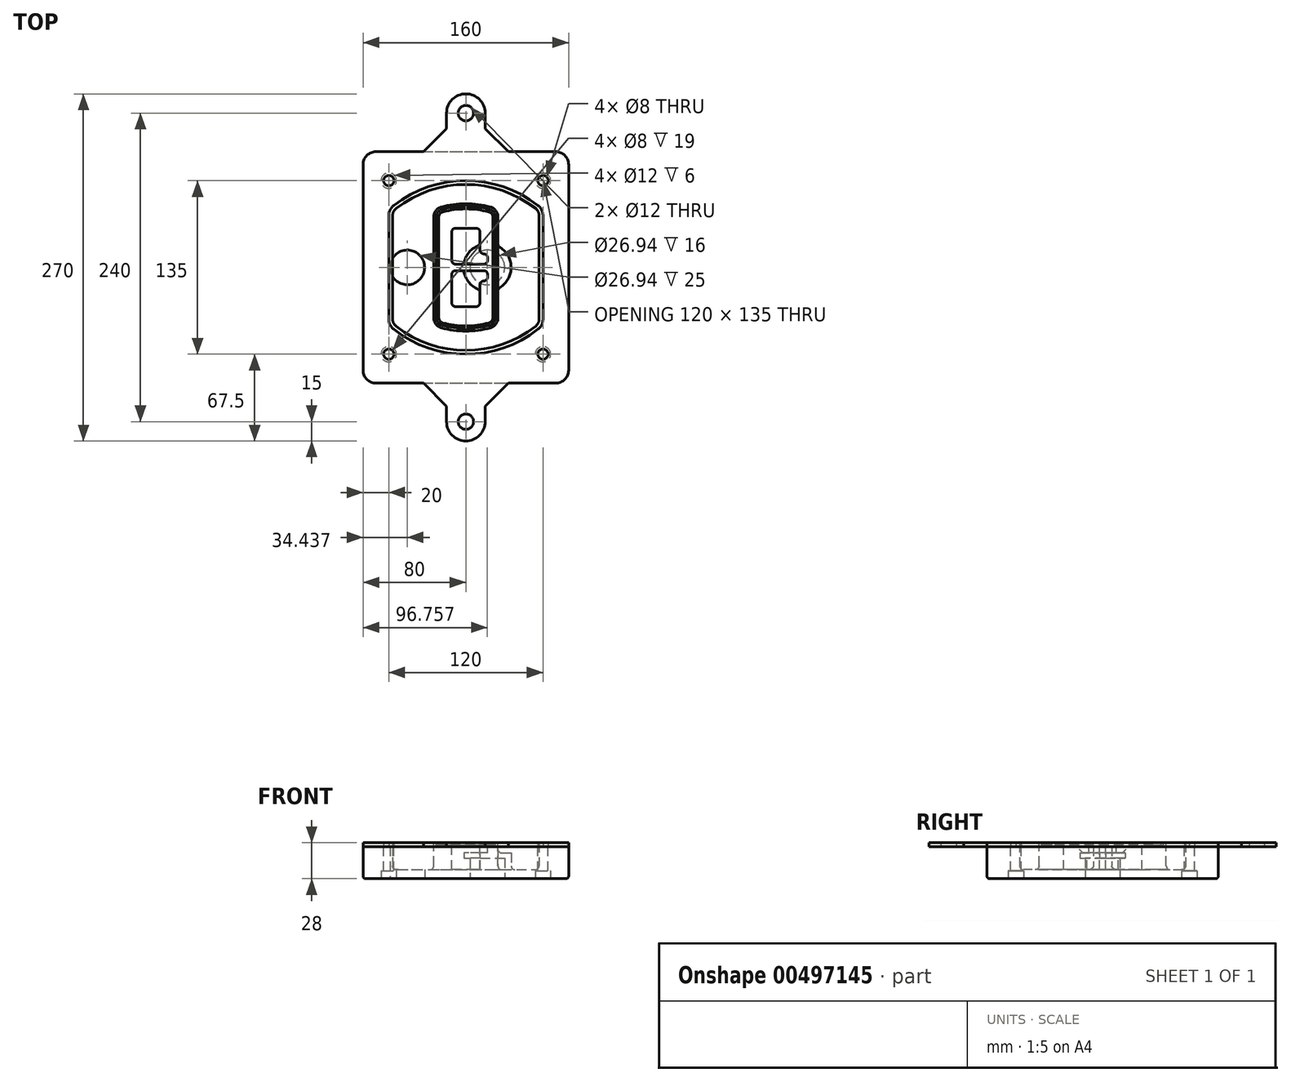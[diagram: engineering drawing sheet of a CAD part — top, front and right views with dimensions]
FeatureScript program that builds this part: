
annotation { "Feature Type Name" : "Feature", "Feature Type Description" : "" }
export const myFeature = defineFeature(function(context is Context, id is Id, definition is map)
    precondition{}
    {
        {
            var Q0;
            Q0=qCreatedBy(makeId("Top.planeOp"),FACE);
            var sketch = newSketch(context, id + "F0", { "sketchPlane" : qUnion([Q0])});
            skPoint(sketch, "E0.rect.middle", {"position": v(0, 0) * mm});
            skLineSegment(sketch, "E1.bottom", {"start": v(-70, -90) * mm, "end": v(70, -90) * mm});
            skLineSegment(sketch, "E1.top", {"start": v(-70, 90) * mm, "end": v(70, 90) * mm});
            skLineSegment(sketch, "E1.left", {"start": v(-80, -80) * mm, "end": v(-80, 80) * mm});
            skLineSegment(sketch, "E1.right", {"start": v(80, -80) * mm, "end": v(80, 80) * mm});
            skLineSegment(sketch, "E2", {"start": v(-80, 90) * mm, "end": v(80, -90) * mm, "construction": true});
            skLineSegment(sketch, "E3", {"start": v(80, 90) * mm, "end": v(-80, -90) * mm, "construction": true});
            skCircle(sketch, "E4", {"center": v(-60, 67.5) * mm, "radius": 4 * mm});
            skCircle(sketch, "E5", {"center": v(60, 67.5) * mm, "radius": 4 * mm});
            skCircle(sketch, "E6", {"center": v(60, -67.5) * mm, "radius": 4 * mm});
            skCircle(sketch, "E7", {"center": v(-60, -67.5) * mm, "radius": 4 * mm});
            skLineSegment(sketch, "E8", {"start": v(-60, 67.5) * mm, "end": v(60, 67.5) * mm, "construction": true});
            skLineSegment(sketch, "E9", {"start": v(60, 67.5) * mm, "end": v(60, -67.5) * mm, "construction": true});
            skLineSegment(sketch, "E10", {"start": v(60, -67.5) * mm, "end": v(-60, -67.5) * mm, "construction": true});
            skLineSegment(sketch, "E11", {"start": v(-60, -67.5) * mm, "end": v(-60, 67.5) * mm, "construction": true});
            skLineSegment(sketch, "E12", {"start": v(-60, 40.3) * mm, "end": v(-60, -40.3) * mm});
            skLineSegment(sketch, "E13", {"start": v(60, 40.3) * mm, "end": v(60, -40.3) * mm});
            skArc(sketch, "E14", {"start": v(56.15, 48.18) * mm, "mid": v(0, 67.5) * mm, "end": v(-56.15, 48.18) * mm});
            skArc(sketch, "E15", {"start": v(-56.15, -48.18) * mm, "mid": v(0, -67.5) * mm, "end": v(56.15, -48.18) * mm});
            skLineSegment(sketch, "E16", {"start": v(-60, 0) * mm, "end": v(60, 0) * mm, "construction": true});
            skPoint(sketch, "E17.visualSharp", {"position": v(-60, -45) * mm});
            skArc(sketch, "E17.filletArc", {"start": v(-60, -40.3) * mm, "mid": v(-58.99, -44.68) * mm, "end": v(-56.15, -48.18) * mm});
            skPoint(sketch, "E18.visualSharp", {"position": v(-60, 45) * mm});
            skArc(sketch, "E18.filletArc", {"start": v(-56.15, 48.18) * mm, "mid": v(-58.99, 44.68) * mm, "end": v(-60, 40.3) * mm});
            skPoint(sketch, "E19.visualSharp", {"position": v(60, 45) * mm});
            skArc(sketch, "E19.filletArc", {"start": v(60, 40.3) * mm, "mid": v(58.99, 44.68) * mm, "end": v(56.15, 48.18) * mm});
            skPoint(sketch, "E20.visualSharp", {"position": v(60, -45) * mm});
            skArc(sketch, "E20.filletArc", {"start": v(56.15, -48.18) * mm, "mid": v(58.99, -44.68) * mm, "end": v(60, -40.3) * mm});
            skPoint(sketch, "E21.visualSharp", {"position": v(-80, 90) * mm});
            skArc(sketch, "E21.filletArc", {"start": v(-70, 90) * mm, "mid": v(-77.07, 87.07) * mm, "end": v(-80, 80) * mm});
            skPoint(sketch, "E22.visualSharp", {"position": v(80, 90) * mm});
            skArc(sketch, "E22.filletArc", {"start": v(80, 80) * mm, "mid": v(77.07, 87.07) * mm, "end": v(70, 90) * mm});
            skPoint(sketch, "E23.visualSharp", {"position": v(80, -90) * mm});
            skArc(sketch, "E23.filletArc", {"start": v(70, -90) * mm, "mid": v(77.07, -87.07) * mm, "end": v(80, -80) * mm});
            skPoint(sketch, "E24.visualSharp", {"position": v(-80, -90) * mm});
            skArc(sketch, "E24.filletArc", {"start": v(-80, -80) * mm, "mid": v(-77.07, -87.07) * mm, "end": v(-70, -90) * mm});
            skArc(sketch, "E25.0", {"start": v(57, 40.3) * mm, "mid": v(56.3, 43.36) * mm, "end": v(54.3, 45.81) * mm});
            skLineSegment(sketch, "E25.1", {"start": v(57, 40.3) * mm, "end": v(57, -40.3) * mm});
            skArc(sketch, "E25.2", {"start": v(54.3, -45.81) * mm, "mid": v(56.3, -43.36) * mm, "end": v(57, -40.3) * mm});
            skArc(sketch, "E25.3", {"start": v(-54.3, -45.81) * mm, "mid": v(0, -64.5) * mm, "end": v(54.3, -45.81) * mm});
            skArc(sketch, "E25.4", {"start": v(-57, -40.3) * mm, "mid": v(-56.3, -43.36) * mm, "end": v(-54.3, -45.81) * mm});
            skArc(sketch, "E25.5", {"start": v(54.3, 45.81) * mm, "mid": v(0, 64.5) * mm, "end": v(-54.3, 45.81) * mm});
            skLineSegment(sketch, "E25.6", {"start": v(-57, 40.3) * mm, "end": v(-57, -40.3) * mm});
            skArc(sketch, "E25.7", {"start": v(-54.3, 45.81) * mm, "mid": v(-56.3, 43.36) * mm, "end": v(-57, 40.3) * mm});
            skArc(sketch, "E26.0", {"start": v(-58.62, 51.33) * mm, "mid": v(-62.58, 46.43) * mm, "end": v(-64, 40.3) * mm});
            skArc(sketch, "E26.1", {"start": v(58.62, 51.33) * mm, "mid": v(0, 71.5) * mm, "end": v(-58.62, 51.33) * mm});
            skArc(sketch, "E26.2", {"start": v(64, 40.3) * mm, "mid": v(62.58, 46.43) * mm, "end": v(58.62, 51.33) * mm});
            skLineSegment(sketch, "E26.3", {"start": v(64, 40.3) * mm, "end": v(64, -40.3) * mm});
            skArc(sketch, "E26.4", {"start": v(58.62, -51.33) * mm, "mid": v(62.58, -46.43) * mm, "end": v(64, -40.3) * mm});
            skLineSegment(sketch, "E26.5", {"start": v(-64, 40.3) * mm, "end": v(-64, -40.3) * mm});
            skArc(sketch, "E26.6", {"start": v(-58.62, -51.33) * mm, "mid": v(0, -71.5) * mm, "end": v(58.62, -51.33) * mm});
            skArc(sketch, "E26.7", {"start": v(-64, -40.3) * mm, "mid": v(-62.58, -46.43) * mm, "end": v(-58.62, -51.33) * mm});
            skSolve(sketch);
        }
        {
            var Q0;
            Q0=makeQuery(id+"F0.imprint","IMPRINT",FACE,{"disambiguationData":[TD([[makeQuery(id+"F0.imprint","IMPRINT",EDGE,{"derivedFrom":sQuery(id+"F0.wireOp",EDGE,"E1.bottom")}),1.0]])]});
            var Q1;
            Q1=makeQuery(id+"F0.imprint","IMPRINT",FACE,{"disambiguationData":[TD([[makeQuery(id+"F0.imprint","IMPRINT",EDGE,{"derivedFrom":sQuery(id+"F0.wireOp",EDGE,"E12")}),1.0]])]});
            var Q2;
            Q2=makeQuery(id+"F0.imprint","IMPRINT",FACE,{"disambiguationData":[TD([[makeQuery(id+"F0.imprint","IMPRINT",EDGE,{"derivedFrom":sQuery(id+"F0.wireOp",EDGE,"E25.0")}),1.0]])]});
            var Q3;
            Q3=makeQuery(id+"F0.imprint","IMPRINT",FACE,{"disambiguationData":[TD([[makeQuery(id+"F0.imprint","IMPRINT",EDGE,{"derivedFrom":sQuery(id+"F0.wireOp",EDGE,"E12")}),-1.0]])]});
            extrude(context, id + "F1", {"entities" : qUnion([Q0, Q1, Q2, Q3]), "oppositeDirection" : true, "depth" : 25 * mm});
        }
        {
            var Q0;
            Q0=makeQuery(id+"F0.imprint","IMPRINT",FACE,{"disambiguationData":[TD([[makeQuery(id+"F0.imprint","IMPRINT",EDGE,{"derivedFrom":sQuery(id+"F0.wireOp",EDGE,"E12")}),1.0]])]});
            extrude(context, id + "F2", {"entities" : qUnion([Q0]), "operationType" : NewBodyOperationType.ADD, "depth" : 3 * mm});
        }
        {
            var Q0;
            Q0=makeQuery(id+"F0.imprint","IMPRINT",FACE,{"disambiguationData":[TD([[makeQuery(id+"F0.imprint","IMPRINT",EDGE,{"derivedFrom":sQuery(id+"F0.wireOp",EDGE,"E25.0")}),1.0]])]});
            extrude(context, id + "F3", {"entities" : qUnion([Q0]), "operationType" : NewBodyOperationType.REMOVE, "oppositeDirection" : true, "depth" : 18 * mm});
        }
        {
            var Q0;
            Q0=makeQuery(id+"F2.opExtrude","CAP_FACE",FACE,{"disambiguationData":[OSD([sQuery(id+"F0.wireOp",EDGE,"E12"),sQuery(id+"F0.wireOp",EDGE,"E13"),sQuery(id+"F0.wireOp",EDGE,"E14"),sQuery(id+"F0.wireOp",EDGE,"E15"),sQuery(id+"F0.wireOp",EDGE,"E17.filletArc"),sQuery(id+"F0.wireOp",EDGE,"E18.filletArc"),sQuery(id+"F0.wireOp",EDGE,"E19.filletArc"),sQuery(id+"F0.wireOp",EDGE,"E20.filletArc"),sQuery(id+"F0.wireOp",EDGE,"E25.0"),sQuery(id+"F0.wireOp",EDGE,"E25.1"),sQuery(id+"F0.wireOp",EDGE,"E25.2"),sQuery(id+"F0.wireOp",EDGE,"E25.3"),sQuery(id+"F0.wireOp",EDGE,"E25.4"),sQuery(id+"F0.wireOp",EDGE,"E25.5"),sQuery(id+"F0.wireOp",EDGE,"E25.6"),sQuery(id+"F0.wireOp",EDGE,"E25.7")])],"isStart":false});
            var sketch = newSketch(context, id + "F4", { "sketchPlane" : qUnion([Q0])});
            skArc(sketch, "E27.0", {"start": v(-19.08, -46.97) * mm, "mid": v(0, -49.5) * mm, "end": v(19.08, -46.97) * mm});
            skArc(sketch, "E28.0", {"start": v(19.08, 46.97) * mm, "mid": v(0, 49.5) * mm, "end": v(-19.08, 46.97) * mm});
            skLineSegment(sketch, "E29", {"start": v(-25, 39.25) * mm, "end": v(-25, -39.25) * mm});
            skLineSegment(sketch, "E30", {"start": v(25, 39.25) * mm, "end": v(25, -39.25) * mm});
            skLineSegment(sketch, "E31", {"start": v(-25, 45.1) * mm, "end": v(25, 45.1) * mm, "construction": true});
            skLineSegment(sketch, "E32", {"start": v(-25, -45.1) * mm, "end": v(25, -45.1) * mm, "construction": true});
            skPoint(sketch, "E33.visualSharp", {"position": v(-25, 45.1) * mm});
            skArc(sketch, "E33.filletArc", {"start": v(-19.08, 46.97) * mm, "mid": v(-23.35, 44.11) * mm, "end": v(-25, 39.25) * mm});
            skPoint(sketch, "E34.visualSharp", {"position": v(25, 45.1) * mm});
            skArc(sketch, "E34.filletArc", {"start": v(25, 39.25) * mm, "mid": v(23.35, 44.11) * mm, "end": v(19.08, 46.97) * mm});
            skPoint(sketch, "E35.visualSharp", {"position": v(25, -45.1) * mm});
            skArc(sketch, "E35.filletArc", {"start": v(19.08, -46.97) * mm, "mid": v(23.35, -44.11) * mm, "end": v(25, -39.25) * mm});
            skPoint(sketch, "E36.visualSharp", {"position": v(-25, -45.1) * mm});
            skArc(sketch, "E36.filletArc", {"start": v(-25, -39.25) * mm, "mid": v(-23.35, -44.11) * mm, "end": v(-19.08, -46.97) * mm});
            skArc(sketch, "E37.0", {"start": v(54.3, 45.81) * mm, "mid": v(0, 64.5) * mm, "end": v(-54.3, 45.81) * mm});
            skArc(sketch, "E37.1", {"start": v(-54.3, 45.81) * mm, "mid": v(-56.3, 43.36) * mm, "end": v(-57, 40.3) * mm});
            skLineSegment(sketch, "E37.2", {"start": v(-57, 40.3) * mm, "end": v(-57, -40.3) * mm});
            skArc(sketch, "E37.3", {"start": v(-57, -40.3) * mm, "mid": v(-56.3, -43.36) * mm, "end": v(-54.3, -45.81) * mm});
            skArc(sketch, "E37.4", {"start": v(-54.3, -45.81) * mm, "mid": v(0, -64.5) * mm, "end": v(54.3, -45.81) * mm});
            skArc(sketch, "E37.5", {"start": v(54.3, -45.81) * mm, "mid": v(56.3, -43.36) * mm, "end": v(57, -40.3) * mm});
            skLineSegment(sketch, "E37.6", {"start": v(57, 40.3) * mm, "end": v(57, -40.3) * mm});
            skArc(sketch, "E37.7", {"start": v(57, 40.3) * mm, "mid": v(56.3, 43.36) * mm, "end": v(54.3, 45.81) * mm});
            skLineSegment(sketch, "E38.0", {"start": v(23, 39.25) * mm, "end": v(23, -39.25) * mm});
            skArc(sketch, "E38.1", {"start": v(18.56, -45.04) * mm, "mid": v(21.76, -42.9) * mm, "end": v(23, -39.25) * mm});
            skArc(sketch, "E38.2", {"start": v(-18.56, -45.04) * mm, "mid": v(0, -47.5) * mm, "end": v(18.56, -45.04) * mm});
            skArc(sketch, "E38.3", {"start": v(-23, -39.25) * mm, "mid": v(-21.76, -42.9) * mm, "end": v(-18.56, -45.04) * mm});
            skLineSegment(sketch, "E38.4", {"start": v(-23, 39.25) * mm, "end": v(-23, -39.25) * mm});
            skArc(sketch, "E38.5", {"start": v(23, 39.25) * mm, "mid": v(21.76, 42.9) * mm, "end": v(18.56, 45.04) * mm});
            skArc(sketch, "E38.6", {"start": v(-18.56, 45.04) * mm, "mid": v(-21.76, 42.9) * mm, "end": v(-23, 39.25) * mm});
            skArc(sketch, "E38.7", {"start": v(18.56, 45.04) * mm, "mid": v(0, 47.5) * mm, "end": v(-18.56, 45.04) * mm});
            skArc(sketch, "E39.0", {"start": v(21, 39.25) * mm, "mid": v(20.18, 41.68) * mm, "end": v(18.04, 43.1) * mm});
            skLineSegment(sketch, "E39.1", {"start": v(21, 39.25) * mm, "end": v(21, -39.25) * mm});
            skArc(sketch, "E39.2", {"start": v(18.04, -43.1) * mm, "mid": v(20.18, -41.68) * mm, "end": v(21, -39.25) * mm});
            skArc(sketch, "E39.3", {"start": v(-18.04, -43.1) * mm, "mid": v(0, -45.5) * mm, "end": v(18.04, -43.1) * mm});
            skArc(sketch, "E39.4", {"start": v(-21, -39.25) * mm, "mid": v(-20.18, -41.68) * mm, "end": v(-18.04, -43.1) * mm});
            skArc(sketch, "E39.5", {"start": v(18.04, 43.1) * mm, "mid": v(0, 45.5) * mm, "end": v(-18.04, 43.1) * mm});
            skLineSegment(sketch, "E39.6", {"start": v(-21, 39.25) * mm, "end": v(-21, -39.25) * mm});
            skArc(sketch, "E39.7", {"start": v(-18.04, 43.1) * mm, "mid": v(-20.18, 41.68) * mm, "end": v(-21, 39.25) * mm});
            skLineSegment(sketch, "E40", {"start": v(-25, 0) * mm, "end": v(25, 0) * mm, "construction": true});
            skLineSegment(sketch, "E41", {"start": v(-11, 5.5) * mm, "end": v(-11, 27.5) * mm});
            skLineSegment(sketch, "E42", {"start": v(-8, 30.5) * mm, "end": v(8, 30.5) * mm});
            skLineSegment(sketch, "E43", {"start": v(11, 27.5) * mm, "end": v(11, 13.5) * mm});
            skLineSegment(sketch, "E44", {"start": v(14, 10.5) * mm, "end": v(14, 10.5) * mm});
            skLineSegment(sketch, "E45", {"start": v(17, 7.5) * mm, "end": v(17, 5.5) * mm});
            skLineSegment(sketch, "E46", {"start": v(14, 2.5) * mm, "end": v(-8, 2.5) * mm});
            skPoint(sketch, "E47.visualSharp", {"position": v(-11, 30.5) * mm});
            skArc(sketch, "E47.filletArc", {"start": v(-8, 30.5) * mm, "mid": v(-10.12, 29.62) * mm, "end": v(-11, 27.5) * mm});
            skPoint(sketch, "E48.visualSharp", {"position": v(11, 30.5) * mm});
            skArc(sketch, "E48.filletArc", {"start": v(11, 27.5) * mm, "mid": v(10.12, 29.62) * mm, "end": v(8, 30.5) * mm});
            skPoint(sketch, "E49.visualSharp", {"position": v(11, 10.5) * mm});
            skArc(sketch, "E49.filletArc", {"start": v(11, 13.5) * mm, "mid": v(11.88, 11.38) * mm, "end": v(14, 10.5) * mm});
            skPoint(sketch, "E50.visualSharp", {"position": v(17, 10.5) * mm});
            skArc(sketch, "E50.filletArc", {"start": v(17, 7.5) * mm, "mid": v(16.12, 9.62) * mm, "end": v(14, 10.5) * mm});
            skPoint(sketch, "E51.visualSharp", {"position": v(17, 2.5) * mm});
            skArc(sketch, "E51.filletArc", {"start": v(14, 2.5) * mm, "mid": v(16.12, 3.38) * mm, "end": v(17, 5.5) * mm});
            skPoint(sketch, "E52.visualSharp", {"position": v(-11, 2.5) * mm});
            skArc(sketch, "E52.filletArc", {"start": v(-11, 5.5) * mm, "mid": v(-10.12, 3.38) * mm, "end": v(-8, 2.5) * mm});
            skLineSegment(sketch, "E53.0.MirrorCS", {"start": v(14, -2.5) * mm, "end": v(-8, -2.5) * mm});
            skArc(sketch, "E54.0.MirrorCS", {"start": v(-11, -5.5) * mm, "mid": v(-10.12, -3.38) * mm, "end": v(-8, -2.5) * mm});
            skLineSegment(sketch, "E55.0.MirrorCS", {"start": v(-11, -5.5) * mm, "end": v(-11, -27.5) * mm});
            skArc(sketch, "E56.0.MirrorCS", {"start": v(-8, -30.5) * mm, "mid": v(-10.12, -29.62) * mm, "end": v(-11, -27.5) * mm});
            skLineSegment(sketch, "E57.0.MirrorCS", {"start": v(-8, -30.5) * mm, "end": v(8, -30.5) * mm});
            skArc(sketch, "E58.0.MirrorCS", {"start": v(11, -27.5) * mm, "mid": v(10.12, -29.62) * mm, "end": v(8, -30.5) * mm});
            skLineSegment(sketch, "E59.0.MirrorCS", {"start": v(11, -27.5) * mm, "end": v(11, -13.5) * mm});
            skArc(sketch, "E60.0.MirrorCS", {"start": v(11, -13.5) * mm, "mid": v(11.88, -11.38) * mm, "end": v(14, -10.5) * mm});
            skArc(sketch, "E61.0.MirrorCS", {"start": v(17, -7.5) * mm, "mid": v(16.12, -9.62) * mm, "end": v(14, -10.5) * mm});
            skLineSegment(sketch, "E62.0.MirrorCS", {"start": v(17, -7.5) * mm, "end": v(17, -5.5) * mm});
            skArc(sketch, "E63.0.MirrorCS", {"start": v(14, -2.5) * mm, "mid": v(16.12, -3.38) * mm, "end": v(17, -5.5) * mm});
            skSolve(sketch);
        }
        {
            var Q0;
            Q0=makeQuery(id+"F4.imprint","IMPRINT",FACE,{"disambiguationData":[TD([[makeQuery(id+"F4.imprint","IMPRINT",EDGE,{"derivedFrom":sQuery(id+"F4.wireOp",EDGE,"E27.0")}),1.0]])]});
            var Q1;
            Q1=makeQuery(id+"F4.imprint","IMPRINT",FACE,{"disambiguationData":[TD([[makeQuery(id+"F4.imprint","IMPRINT",EDGE,{"derivedFrom":sQuery(id+"F4.wireOp",EDGE,"E38.0")}),-1.0]])]});
            var Q2;
            Q2=makeQuery(id+"F4.imprint","IMPRINT",FACE,{"disambiguationData":[TD([[makeQuery(id+"F4.imprint","IMPRINT",EDGE,{"derivedFrom":sQuery(id+"F4.wireOp",EDGE,"E39.0")}),1.0]])]});
            extrude(context, id + "F5", {"entities" : qUnion([Q0, Q1, Q2]), "operationType" : NewBodyOperationType.ADD, "endBound" : BoundingType.UP_TO_NEXT, "oppositeDirection" : true, "depth" : 25 * mm});
        }
        {
            var Q0;
            Q0=makeQuery(id+"F4.imprint","IMPRINT",FACE,{"disambiguationData":[TD([[makeQuery(id+"F4.imprint","IMPRINT",EDGE,{"derivedFrom":sQuery(id+"F4.wireOp",EDGE,"E38.0")}),-1.0]])]});
            extrude(context, id + "F6", {"entities" : qUnion([Q0]), "operationType" : NewBodyOperationType.REMOVE, "oppositeDirection" : true, "depth" : 2 * mm});
        }
        {
            var Q0;
            Q0=makeQuery(id+"F1.opExtrude","CAP_FACE",FACE,{"disambiguationData":[OSD([sQuery(id+"F0.wireOp",EDGE,"E1.bottom"),sQuery(id+"F0.wireOp",EDGE,"E1.top"),sQuery(id+"F0.wireOp",EDGE,"E1.left"),sQuery(id+"F0.wireOp",EDGE,"E1.right"),sQuery(id+"F0.wireOp",EDGE,"E4"),sQuery(id+"F0.wireOp",EDGE,"E5"),sQuery(id+"F0.wireOp",EDGE,"E6"),sQuery(id+"F0.wireOp",EDGE,"E7"),sQuery(id+"F0.wireOp",EDGE,"E21.filletArc"),sQuery(id+"F0.wireOp",EDGE,"E22.filletArc"),sQuery(id+"F0.wireOp",EDGE,"E23.filletArc"),sQuery(id+"F0.wireOp",EDGE,"E24.filletArc")])],"isStart":false});
            var sketch = newSketch(context, id + "F7", { "sketchPlane" : qUnion([Q0])});
            skCircle(sketch, "E64", {"center": v(16.76, 0) * mm, "radius": 13.47 * mm});
            skCircle(sketch, "E65", {"center": v(-45.56, 0) * mm, "radius": 13.47 * mm});
            skLineSegment(sketch, "E66", {"start": v(80, 0) * mm, "end": v(-80, 0) * mm});
            skCircle(sketch, "E67", {"center": v(16.76, 0) * mm, "radius": 18.47 * mm});
            skCircle(sketch, "E68", {"center": v(60, -67.5) * mm, "radius": 6 * mm});
            skCircle(sketch, "E69", {"center": v(-60, -67.5) * mm, "radius": 6 * mm});
            skCircle(sketch, "E70", {"center": v(-60, 67.5) * mm, "radius": 6 * mm});
            skCircle(sketch, "E71", {"center": v(60, 67.5) * mm, "radius": 6 * mm});
            skSolve(sketch);
        }
        {
            var Q0;
            {var subQ1=sQuery(id+"F7.wireOp",EDGE,"E66");var subQ4=sQuery(id+"F7.wireOp",EDGE,"E64");var subQ6=makeQuery(id+"F7.imprint","INTERSECT",VERTEX,{"disambiguationData":[OD(0.0)],"derivedFrom":[subQ4,subQ1]});Q0=makeQuery(id+"F7.imprint","IMPRINT",FACE,{"disambiguationData":[TD([[makeQuery(id+"F7.imprint","IMPRINT",EDGE,{"disambiguationData":[TD([[subQ6,-1.0]])],"derivedFrom":subQ4}),-1.0]])]});}
            var Q1;
            {var subQ0=sQuery(id+"F7.wireOp",EDGE,"E66");var subQ1=sQuery(id+"F7.wireOp",EDGE,"E64");var subQ3=makeQuery(id+"F7.imprint","INTERSECT",VERTEX,{"disambiguationData":[OD(0.0)],"derivedFrom":[subQ1,subQ0]});Q1=makeQuery(id+"F7.imprint","IMPRINT",FACE,{"disambiguationData":[TD([[makeQuery(id+"F7.imprint","IMPRINT",EDGE,{"disambiguationData":[TD([[subQ3,-1.0]])],"derivedFrom":subQ1}),1.0]])]});}
            var Q2;
            {var subQ0=sQuery(id+"F7.wireOp",EDGE,"E66");var subQ1=sQuery(id+"F7.wireOp",EDGE,"E64");var subQ3=makeQuery(id+"F7.imprint","INTERSECT",VERTEX,{"disambiguationData":[OD(0.0)],"derivedFrom":[subQ1,subQ0]});Q2=makeQuery(id+"F7.imprint","IMPRINT",FACE,{"disambiguationData":[TD([[makeQuery(id+"F7.imprint","IMPRINT",EDGE,{"disambiguationData":[TD([[subQ3,1.0]])],"derivedFrom":subQ1}),1.0]])]});}
            var Q3;
            {var subQ1=sQuery(id+"F7.wireOp",EDGE,"E66");var subQ4=sQuery(id+"F7.wireOp",EDGE,"E64");var subQ6=makeQuery(id+"F7.imprint","INTERSECT",VERTEX,{"disambiguationData":[OD(0.0)],"derivedFrom":[subQ4,subQ1]});Q3=makeQuery(id+"F7.imprint","IMPRINT",FACE,{"disambiguationData":[TD([[makeQuery(id+"F7.imprint","IMPRINT",EDGE,{"disambiguationData":[TD([[subQ6,1.0]])],"derivedFrom":subQ4}),-1.0]])]});}
            extrude(context, id + "F8", {"entities" : qUnion([Q0, Q1, Q2, Q3]), "operationType" : NewBodyOperationType.ADD, "oppositeDirection" : true, "depth" : 20 * mm});
        }
        {
            var Q0;
            {var subQ0=sQuery(id+"F7.wireOp",EDGE,"E66");var subQ1=sQuery(id+"F7.wireOp",EDGE,"E64");var subQ3=makeQuery(id+"F7.imprint","INTERSECT",VERTEX,{"disambiguationData":[OD(0.0)],"derivedFrom":[subQ1,subQ0]});Q0=makeQuery(id+"F7.imprint","IMPRINT",FACE,{"disambiguationData":[TD([[makeQuery(id+"F7.imprint","IMPRINT",EDGE,{"disambiguationData":[TD([[subQ3,-1.0]])],"derivedFrom":subQ1}),1.0]])]});}
            var Q1;
            {var subQ0=sQuery(id+"F7.wireOp",EDGE,"E66");var subQ1=sQuery(id+"F7.wireOp",EDGE,"E64");var subQ3=makeQuery(id+"F7.imprint","INTERSECT",VERTEX,{"disambiguationData":[OD(0.0)],"derivedFrom":[subQ1,subQ0]});Q1=makeQuery(id+"F7.imprint","IMPRINT",FACE,{"disambiguationData":[TD([[makeQuery(id+"F7.imprint","IMPRINT",EDGE,{"disambiguationData":[TD([[subQ3,1.0]])],"derivedFrom":subQ1}),1.0]])]});}
            extrude(context, id + "F9", {"entities" : qUnion([Q0, Q1]), "operationType" : NewBodyOperationType.REMOVE, "oppositeDirection" : true, "depth" : 16 * mm});
        }
        {
            var Q0;
            {var subQ0=sQuery(id+"F7.wireOp",EDGE,"E66");var subQ1=sQuery(id+"F7.wireOp",EDGE,"E65");var subQ3=makeQuery(id+"F7.imprint","INTERSECT",VERTEX,{"disambiguationData":[OD(0.0)],"derivedFrom":[subQ1,subQ0]});Q0=makeQuery(id+"F7.imprint","IMPRINT",FACE,{"disambiguationData":[TD([[makeQuery(id+"F7.imprint","IMPRINT",EDGE,{"disambiguationData":[TD([[subQ3,-1.0]])],"derivedFrom":subQ1}),1.0]])]});}
            var Q1;
            {var subQ0=sQuery(id+"F7.wireOp",EDGE,"E66");var subQ1=sQuery(id+"F7.wireOp",EDGE,"E65");var subQ3=makeQuery(id+"F7.imprint","INTERSECT",VERTEX,{"disambiguationData":[OD(0.0)],"derivedFrom":[subQ1,subQ0]});Q1=makeQuery(id+"F7.imprint","IMPRINT",FACE,{"disambiguationData":[TD([[makeQuery(id+"F7.imprint","IMPRINT",EDGE,{"disambiguationData":[TD([[subQ3,1.0]])],"derivedFrom":subQ1}),1.0]])]});}
            extrude(context, id + "F10", {"entities" : qUnion([Q0, Q1]), "operationType" : NewBodyOperationType.REMOVE, "oppositeDirection" : true, "depth" : 25 * mm});
        }
        {
            var Q0;
            Q0=makeQuery(id+"F7.imprint","IMPRINT",FACE,{"disambiguationData":[TD([[makeQuery(id+"F7.imprint","IMPRINT",EDGE,{"derivedFrom":sQuery(id+"F7.wireOp",EDGE,"E68")}),1.0]])]});
            var Q1;
            Q1=makeQuery(id+"F7.imprint","IMPRINT",FACE,{"disambiguationData":[TD([[makeQuery(id+"F7.imprint","IMPRINT",EDGE,{"derivedFrom":makeQuery(id+"F1.opExtrude","CAP_EDGE",EDGE,{"disambiguationData":[OSD([sQuery(id+"F0.wireOp",EDGE,"E5")])],"isStart":false})}),-1.0]])]});
            var Q2;
            Q2=makeQuery(id+"F7.imprint","IMPRINT",FACE,{"disambiguationData":[TD([[makeQuery(id+"F7.imprint","IMPRINT",EDGE,{"derivedFrom":sQuery(id+"F7.wireOp",EDGE,"E69")}),1.0]])]});
            var Q3;
            Q3=makeQuery(id+"F7.imprint","IMPRINT",FACE,{"disambiguationData":[TD([[makeQuery(id+"F7.imprint","IMPRINT",EDGE,{"derivedFrom":makeQuery(id+"F1.opExtrude","CAP_EDGE",EDGE,{"disambiguationData":[OSD([sQuery(id+"F0.wireOp",EDGE,"E4")])],"isStart":false})}),-1.0]])]});
            var Q4;
            Q4=makeQuery(id+"F7.imprint","IMPRINT",FACE,{"disambiguationData":[TD([[makeQuery(id+"F7.imprint","IMPRINT",EDGE,{"derivedFrom":sQuery(id+"F7.wireOp",EDGE,"E70")}),1.0]])]});
            var Q5;
            Q5=makeQuery(id+"F7.imprint","IMPRINT",FACE,{"disambiguationData":[TD([[makeQuery(id+"F7.imprint","IMPRINT",EDGE,{"derivedFrom":makeQuery(id+"F1.opExtrude","CAP_EDGE",EDGE,{"disambiguationData":[OSD([sQuery(id+"F0.wireOp",EDGE,"E7")])],"isStart":false})}),-1.0]])]});
            var Q6;
            Q6=makeQuery(id+"F7.imprint","IMPRINT",FACE,{"disambiguationData":[TD([[makeQuery(id+"F7.imprint","IMPRINT",EDGE,{"derivedFrom":sQuery(id+"F7.wireOp",EDGE,"E71")}),1.0]])]});
            var Q7;
            Q7=makeQuery(id+"F7.imprint","IMPRINT",FACE,{"disambiguationData":[TD([[makeQuery(id+"F7.imprint","IMPRINT",EDGE,{"derivedFrom":makeQuery(id+"F1.opExtrude","CAP_EDGE",EDGE,{"disambiguationData":[OSD([sQuery(id+"F0.wireOp",EDGE,"E6")])],"isStart":false})}),-1.0]])]});
            extrude(context, id + "F11", {"entities" : qUnion([Q0, Q1, Q2, Q3, Q4, Q5, Q6, Q7]), "operationType" : NewBodyOperationType.REMOVE, "oppositeDirection" : true, "depth" : 6 * mm});
        }
        {
            var Q0;
            Q0=makeQuery(id+"F9.boolean.opBoolean","COPY",FACE,{"derivedFrom":makeQuery(id+"F9.opExtrude","CAP_FACE",FACE,{"disambiguationData":[OSD([sQuery(id+"F7.wireOp",EDGE,"E64")])],"isStart":false})});
            var sketch = newSketch(context, id + "F12", { "sketchPlane" : qUnion([Q0])});
            skArc(sketch, "E72.0", {"start": v(11, 17.55) * mm, "mid": v(2.57, 11.82) * mm, "end": v(-1.54, 2.5) * mm});
            skArc(sketch, "E72.1", {"start": v(-1.54, -2.5) * mm, "mid": v(2.57, -11.82) * mm, "end": v(11, -17.55) * mm});
            skLineSegment(sketch, "E73", {"start": v(-1.54, -2.5) * mm, "end": v(14, -2.5) * mm});
            skLineSegment(sketch, "E74.0", {"start": v(14, 2.5) * mm, "end": v(-1.54, 2.5) * mm});
            skArc(sketch, "E74.1", {"start": v(14, 2.5) * mm, "mid": v(16.12, 3.38) * mm, "end": v(17, 5.5) * mm});
            skLineSegment(sketch, "E74.2", {"start": v(17, 7.5) * mm, "end": v(17, 5.5) * mm});
            skArc(sketch, "E74.3", {"start": v(17, 7.5) * mm, "mid": v(16.12, 9.62) * mm, "end": v(14, 10.5) * mm});
            skArc(sketch, "E74.4", {"start": v(11, 13.5) * mm, "mid": v(11.88, 11.38) * mm, "end": v(14, 10.5) * mm});
            skLineSegment(sketch, "E74.5", {"start": v(11, 17.55) * mm, "end": v(11, 13.5) * mm});
            skLineSegment(sketch, "E74.7", {"start": v(14, -2.5) * mm, "end": v(-1.54, -2.5) * mm});
            skArc(sketch, "E74.8", {"start": v(14, -2.5) * mm, "mid": v(16.12, -3.38) * mm, "end": v(17, -5.5) * mm});
            skLineSegment(sketch, "E74.9", {"start": v(17, -7.5) * mm, "end": v(17, -5.5) * mm});
            skArc(sketch, "E74.10", {"start": v(17, -7.5) * mm, "mid": v(16.12, -9.62) * mm, "end": v(14, -10.5) * mm});
            skArc(sketch, "E74.11", {"start": v(11, -13.5) * mm, "mid": v(11.88, -11.38) * mm, "end": v(14, -10.5) * mm});
            skLineSegment(sketch, "E74.12", {"start": v(11, -17.55) * mm, "end": v(11, -13.5) * mm});
            skPoint(sketch, "E75.orphan", {"position": v(11, -27.5) * mm});
            skPoint(sketch, "E76.orphan", {"position": v(-8, -2.5) * mm});
            skPoint(sketch, "E77.orphan", {"position": v(-8, 2.5) * mm});
            skPoint(sketch, "E78.orphan", {"position": v(11, 27.5) * mm});
            skSolve(sketch);
        }
        {
            var Q0;
            {var subQ7=sQuery(id+"F12.wireOp",EDGE,"E72.0");var subQ14=sQuery(id+"F12.wireOp",EDGE,"E72.1");var subQ16=sQuery(id+"F12.wireOp",EDGE,"E74.1");var subQ18=sQuery(id+"F12.wireOp",EDGE,"E74.8");Q0=qUnion([makeQuery(id+"F12.imprint","IMPRINT",FACE,{"disambiguationData":[TD([[makeQuery(id+"F12.imprint","IMPRINT",EDGE,{"derivedFrom":subQ7}),1.0]])]}),makeQuery(id+"F12.imprint","IMPRINT",FACE,{"disambiguationData":[TD([[makeQuery(id+"F12.imprint","IMPRINT",EDGE,{"derivedFrom":subQ14}),1.0]])]}),makeQuery(id+"F12.imprint","IMPRINT",FACE,{"disambiguationData":[TD([[makeQuery(id+"F12.imprint","IMPRINT",EDGE,{"derivedFrom":subQ16}),1.0]])]}),makeQuery(id+"F12.imprint","IMPRINT",FACE,{"disambiguationData":[TD([[makeQuery(id+"F12.imprint","IMPRINT",EDGE,{"derivedFrom":subQ18}),-1.0]])]})]);}
            var Q1;
            Q1=makeQuery(id+"F5.boolean.opBoolean","SPLIT",FACE,{"disambiguationData":[TD([makeQuery(id+"F5.opExtrude","SWEPT_FACE",FACE,{"disambiguationData":[OSD([sQuery(id+"F4.wireOp",EDGE,"E41")])]})])],"derivedFrom":makeQuery(id+"F3.boolean.opBoolean","COPY",FACE,{"derivedFrom":makeQuery(id+"F3.opExtrude","CAP_FACE",FACE,{"disambiguationData":[OSD([sQuery(id+"F0.wireOp",EDGE,"E25.0"),sQuery(id+"F0.wireOp",EDGE,"E25.1"),sQuery(id+"F0.wireOp",EDGE,"E25.2"),sQuery(id+"F0.wireOp",EDGE,"E25.3"),sQuery(id+"F0.wireOp",EDGE,"E25.4"),sQuery(id+"F0.wireOp",EDGE,"E25.5"),sQuery(id+"F0.wireOp",EDGE,"E25.6"),sQuery(id+"F0.wireOp",EDGE,"E25.7")])],"isStart":false})})});
            extrude(context, id + "F13", {"entities" : qUnion([Q0]), "operationType" : NewBodyOperationType.REMOVE, "endBound" : BoundingType.UP_TO_SURFACE, "endBoundEntityFace" : qUnion([Q1]), "depth" : 25 * mm});
        }
        {
            var Q0;
            Q0=makeQuery(id+"F3.boolean.opBoolean","COPY",EDGE,{"derivedFrom":makeQuery(id+"F3.opExtrude","CAP_EDGE",EDGE,{"disambiguationData":[OSD([sQuery(id+"F0.wireOp",EDGE,"E25.6")])],"isStart":false})});
            var Q1;
            Q1=makeQuery(id+"F8.boolean.opBoolean","INTERSECT",EDGE,{"derivedFrom":[makeQuery(id+"F5.opExtrude","SWEPT_FACE",FACE,{"disambiguationData":[OSD([sQuery(id+"F4.wireOp",EDGE,"E30")])]}),makeQuery(id+"F8.opExtrude","CAP_FACE",FACE,{"disambiguationData":[OSD([sQuery(id+"F7.wireOp",EDGE,"E67")])],"isStart":false})]});
            var Q2;
            Q2=makeQuery(id+"F8.boolean.opBoolean","INTERSECT",EDGE,{"disambiguationData":[OD(1.0)],"derivedFrom":[makeQuery(id+"F5.opExtrude","SWEPT_FACE",FACE,{"disambiguationData":[OSD([sQuery(id+"F4.wireOp",EDGE,"E30")])]}),makeQuery(id+"F8.opExtrude","SWEPT_FACE",FACE,{"disambiguationData":[OSD([sQuery(id+"F7.wireOp",EDGE,"E67")])]})]});
            var Q3;
            {var subQ0=sQuery(id+"F4.wireOp",EDGE,"E30");Q3=makeQuery(id+"F8.boolean.opBoolean","SPLIT",EDGE,{"disambiguationData":[TD([makeQuery(id+"F5.opExtrude","SWEPT_FACE",FACE,{"disambiguationData":[OSD([sQuery(id+"F4.wireOp",EDGE,"E35.filletArc")])]})])],"derivedFrom":makeQuery(id+"F5.opExtrude","CAP_EDGE",EDGE,{"disambiguationData":[OSD([subQ0])],"isStart":false})});}
            var Q4;
            {var subQ0=sQuery(id+"F0.wireOp",EDGE,"E25.7");var subQ1=sQuery(id+"F0.wireOp",EDGE,"E25.1");var subQ2=sQuery(id+"F0.wireOp",EDGE,"E25.6");var subQ3=sQuery(id+"F0.wireOp",EDGE,"E25.5");var subQ4=sQuery(id+"F0.wireOp",EDGE,"E25.4");var subQ5=sQuery(id+"F0.wireOp",EDGE,"E25.0");var subQ6=sQuery(id+"F0.wireOp",EDGE,"E25.2");var subQ7=sQuery(id+"F0.wireOp",EDGE,"E25.3");Q4=makeQuery(id+"F8.boolean.opBoolean","INTERSECT",EDGE,{"derivedFrom":[makeQuery(id+"F5.boolean.opBoolean","SPLIT",FACE,{"disambiguationData":[TD([makeQuery(id+"F2.opExtrude","SWEPT_FACE",FACE,{"disambiguationData":[OSD([subQ5])]})])],"derivedFrom":makeQuery(id+"F3.boolean.opBoolean","COPY",FACE,{"derivedFrom":makeQuery(id+"F3.opExtrude","CAP_FACE",FACE,{"disambiguationData":[OSD([subQ5,subQ1,subQ6,subQ7,subQ4,subQ3,subQ2,subQ0])],"isStart":false})})}),makeQuery(id+"F8.opExtrude","SWEPT_FACE",FACE,{"disambiguationData":[OSD([sQuery(id+"F7.wireOp",EDGE,"E67")])]})]});}
            var Q5;
            Q5=makeQuery(id+"F8.boolean.opBoolean","INTERSECT",EDGE,{"disambiguationData":[OD(0.0)],"derivedFrom":[makeQuery(id+"F5.opExtrude","SWEPT_FACE",FACE,{"disambiguationData":[OSD([sQuery(id+"F4.wireOp",EDGE,"E30")])]}),makeQuery(id+"F8.opExtrude","SWEPT_FACE",FACE,{"disambiguationData":[OSD([sQuery(id+"F7.wireOp",EDGE,"E67")])]})]});
            fillet(context, id + "F14", {"entities" : qUnion([Q0, Q1, Q2, Q3, Q4, Q5]), "radius" : 3 * mm, "tangentPropagation" : true, "allowEdgeOverflow" : false});
        }
        {
            var Q0;
            Q0=makeQuery(id+"F1.opExtrude","CAP_EDGE",EDGE,{"disambiguationData":[OSD([sQuery(id+"F0.wireOp",EDGE,"E1.bottom")])],"isStart":false});
            fillet(context, id + "F15", {"entities" : qUnion([Q0]), "radius" : 2 * mm, "tangentPropagation" : true, "allowEdgeOverflow" : false});
        }
        {
            var Q0;
            {var subQ0=sQuery(id+"F0.wireOp",EDGE,"E21.filletArc");var subQ1=sQuery(id+"F0.wireOp",EDGE,"E7");var subQ2=sQuery(id+"F0.wireOp",EDGE,"E6");var subQ3=sQuery(id+"F0.wireOp",EDGE,"E5");var subQ4=sQuery(id+"F0.wireOp",EDGE,"E4");var subQ5=sQuery(id+"F0.wireOp",EDGE,"E22.filletArc");var subQ6=sQuery(id+"F0.wireOp",EDGE,"E1.bottom");var subQ7=sQuery(id+"F0.wireOp",EDGE,"E1.right");var subQ8=sQuery(id+"F0.wireOp",EDGE,"E1.top");var subQ9=sQuery(id+"F0.wireOp",EDGE,"E1.left");var subQ10=sQuery(id+"F0.wireOp",EDGE,"E23.filletArc");var subQ11=sQuery(id+"F0.wireOp",EDGE,"E24.filletArc");Q0=makeQuery(id+"F2.boolean.opBoolean","SPLIT",FACE,{"disambiguationData":[TD([makeQuery(id+"F1.opExtrude","SWEPT_FACE",FACE,{"disambiguationData":[OSD([subQ6])]})])],"derivedFrom":makeQuery(id+"F1.opExtrude","CAP_FACE",FACE,{"disambiguationData":[OSD([subQ6,subQ8,subQ9,subQ7,subQ4,subQ3,subQ2,subQ1,subQ0,subQ5,subQ10,subQ11])],"isStart":true})});}
            var sketch = newSketch(context, id + "F16", { "sketchPlane" : qUnion([Q0])});
            skArc(sketch, "E79.0", {"start": v(-70, 90) * mm, "mid": v(-77.07, 87.07) * mm, "end": v(-80, 80) * mm});
            skLineSegment(sketch, "E79.1", {"start": v(-70, 90) * mm, "end": v(70, 90) * mm});
            skLineSegment(sketch, "E79.2", {"start": v(-80, -80) * mm, "end": v(-80, 80) * mm});
            skArc(sketch, "E79.3", {"start": v(-80, -80) * mm, "mid": v(-77.07, -87.07) * mm, "end": v(-70, -90) * mm});
            skLineSegment(sketch, "E79.4", {"start": v(-70, -90) * mm, "end": v(70, -90) * mm});
            skArc(sketch, "E79.5", {"start": v(70, -90) * mm, "mid": v(77.07, -87.07) * mm, "end": v(80, -80) * mm});
            skLineSegment(sketch, "E79.6", {"start": v(80, -80) * mm, "end": v(80, 80) * mm});
            skArc(sketch, "E79.7", {"start": v(80, 80) * mm, "mid": v(77.07, 87.07) * mm, "end": v(70, 90) * mm});
            skCircle(sketch, "E79.8", {"center": v(60, 67.5) * mm, "radius": 4 * mm});
            skCircle(sketch, "E79.9", {"center": v(60, -67.5) * mm, "radius": 4 * mm});
            skCircle(sketch, "E79.10", {"center": v(-60, -67.5) * mm, "radius": 4 * mm});
            skCircle(sketch, "E79.11", {"center": v(-60, 67.5) * mm, "radius": 4 * mm});
            skArc(sketch, "E79.12", {"start": v(56.15, 48.18) * mm, "mid": v(0, 67.5) * mm, "end": v(-56.15, 48.18) * mm});
            skArc(sketch, "E79.13", {"start": v(-56.15, 48.18) * mm, "mid": v(-58.99, 44.68) * mm, "end": v(-60, 40.3) * mm});
            skLineSegment(sketch, "E79.14", {"start": v(-60, 40.3) * mm, "end": v(-60, -40.3) * mm});
            skArc(sketch, "E79.15", {"start": v(-60, -40.3) * mm, "mid": v(-58.99, -44.68) * mm, "end": v(-56.15, -48.18) * mm});
            skArc(sketch, "E79.16", {"start": v(-56.15, -48.18) * mm, "mid": v(0, -67.5) * mm, "end": v(56.15, -48.18) * mm});
            skArc(sketch, "E79.17", {"start": v(56.15, -48.18) * mm, "mid": v(58.99, -44.68) * mm, "end": v(60, -40.3) * mm});
            skLineSegment(sketch, "E79.18", {"start": v(60, 40.3) * mm, "end": v(60, -40.3) * mm});
            skArc(sketch, "E79.19", {"start": v(60, 40.3) * mm, "mid": v(58.99, 44.68) * mm, "end": v(56.15, 48.18) * mm});
            skSolve(sketch);
        }
        {
            var Q0;
            Q0=makeQuery(id+"F16.imprint","IMPRINT",FACE,{"disambiguationData":[TD([[makeQuery(id+"F16.imprint","IMPRINT",EDGE,{"derivedFrom":sQuery(id+"F16.wireOp",EDGE,"E79.0")}),1.0]])]});
            var sketch = newSketch(context, id + "F17", { "sketchPlane" : qUnion([Q0])});
            skLineSegment(sketch, "E80.0", {"start": v(-70, 90) * mm, "end": v(70, 90) * mm});
            skArc(sketch, "E80.1", {"start": v(-70, 90) * mm, "mid": v(-77.07, 87.07) * mm, "end": v(-80, 80) * mm});
            skLineSegment(sketch, "E80.2", {"start": v(-80, -80) * mm, "end": v(-80, 80) * mm});
            skCircle(sketch, "E80.3", {"center": v(-60, 67.5) * mm, "radius": 4 * mm});
            skArc(sketch, "E80.4", {"start": v(80, 80) * mm, "mid": v(77.07, 87.07) * mm, "end": v(70, 90) * mm});
            skLineSegment(sketch, "E80.5", {"start": v(80, -80) * mm, "end": v(80, 80) * mm});
            skArc(sketch, "E80.6", {"start": v(70, -90) * mm, "mid": v(77.07, -87.07) * mm, "end": v(80, -80) * mm});
            skLineSegment(sketch, "E80.7", {"start": v(-70, -90) * mm, "end": v(70, -90) * mm});
            skArc(sketch, "E80.8", {"start": v(-80, -80) * mm, "mid": v(-77.07, -87.07) * mm, "end": v(-70, -90) * mm});
            skArc(sketch, "E80.9", {"start": v(56.15, 48.18) * mm, "mid": v(0, 67.5) * mm, "end": v(-56.15, 48.18) * mm});
            skCircle(sketch, "E80.10", {"center": v(60, 67.5) * mm, "radius": 4 * mm});
            skCircle(sketch, "E80.11", {"center": v(60, -67.5) * mm, "radius": 4 * mm});
            skCircle(sketch, "E80.12", {"center": v(-60, -67.5) * mm, "radius": 4 * mm});
            skArc(sketch, "E80.13", {"start": v(-56.15, 48.18) * mm, "mid": v(-58.99, 44.68) * mm, "end": v(-60, 40.3) * mm});
            skLineSegment(sketch, "E80.14", {"start": v(-60, 40.3) * mm, "end": v(-60, -40.3) * mm});
            skLineSegment(sketch, "E80.15", {"start": v(60, 40.3) * mm, "end": v(60, -40.3) * mm});
            skArc(sketch, "E80.16", {"start": v(-56.15, -48.18) * mm, "mid": v(0, -67.5) * mm, "end": v(56.15, -48.18) * mm});
            skArc(sketch, "E80.17", {"start": v(-60, -40.3) * mm, "mid": v(-58.99, -44.68) * mm, "end": v(-56.15, -48.18) * mm});
            skArc(sketch, "E80.18", {"start": v(60, 40.3) * mm, "mid": v(58.99, 44.68) * mm, "end": v(56.15, 48.18) * mm});
            skArc(sketch, "E80.19", {"start": v(56.15, -48.18) * mm, "mid": v(58.99, -44.68) * mm, "end": v(60, -40.3) * mm});
            skLineSegment(sketch, "E81", {"start": v(0, 23.75) * mm, "end": v(0, 120) * mm, "construction": true});
            skPoint(sketch, "E81.endSnap0", {"position": v(0, 90) * mm});
            skCircle(sketch, "E82", {"center": v(0, 120) * mm, "radius": 6 * mm});
            skLineSegment(sketch, "E83", {"start": v(33, 90) * mm, "end": v(15, 108) * mm});
            skLineSegment(sketch, "E84", {"start": v(15, 108) * mm, "end": v(15, 120) * mm});
            skArc(sketch, "E85", {"start": v(15, 120) * mm, "mid": v(0, 135) * mm, "end": v(-15, 120) * mm});
            skLineSegment(sketch, "E86", {"start": v(-15, 120) * mm, "end": v(-15, 108) * mm});
            skLineSegment(sketch, "E87", {"start": v(-15, 108) * mm, "end": v(-33, 90) * mm});
            skLineSegment(sketch, "E88", {"start": v(-80, 0) * mm, "end": v(80, 0) * mm, "construction": true});
            skLineSegment(sketch, "E89.MirrorCS", {"start": v(-15, -108) * mm, "end": v(-33, -90) * mm});
            skLineSegment(sketch, "E90.MirrorCS", {"start": v(-15, -120) * mm, "end": v(-15, -108) * mm});
            skArc(sketch, "E91.MirrorCS", {"start": v(15, -120) * mm, "mid": v(0, -135) * mm, "end": v(-15, -120) * mm});
            skLineSegment(sketch, "E92.MirrorCS", {"start": v(15, -108) * mm, "end": v(15, -120) * mm});
            skLineSegment(sketch, "E93.MirrorCS", {"start": v(33, -90) * mm, "end": v(15, -108) * mm});
            skCircle(sketch, "E94.MirrorC", {"center": v(0, -120) * mm, "radius": 6 * mm});
            skLineSegment(sketch, "E95.MirrorCS", {"start": v(0, -23.75) * mm, "end": v(0, -120) * mm, "construction": true});
            skSolve(sketch);
        }
        {
            var Q0;
            Q0 = qSketchRegion(id + "F17", true);
            var Q1;
            Q1=makeQuery(id+"F2.opExtrude","CAP_FACE",FACE,{"disambiguationData":[OSD([sQuery(id+"F0.wireOp",EDGE,"E12"),sQuery(id+"F0.wireOp",EDGE,"E13"),sQuery(id+"F0.wireOp",EDGE,"E14"),sQuery(id+"F0.wireOp",EDGE,"E15"),sQuery(id+"F0.wireOp",EDGE,"E17.filletArc"),sQuery(id+"F0.wireOp",EDGE,"E18.filletArc"),sQuery(id+"F0.wireOp",EDGE,"E19.filletArc"),sQuery(id+"F0.wireOp",EDGE,"E20.filletArc"),sQuery(id+"F0.wireOp",EDGE,"E25.0"),sQuery(id+"F0.wireOp",EDGE,"E25.1"),sQuery(id+"F0.wireOp",EDGE,"E25.2"),sQuery(id+"F0.wireOp",EDGE,"E25.3"),sQuery(id+"F0.wireOp",EDGE,"E25.4"),sQuery(id+"F0.wireOp",EDGE,"E25.5"),sQuery(id+"F0.wireOp",EDGE,"E25.6"),sQuery(id+"F0.wireOp",EDGE,"E25.7")])],"isStart":false});
            extrude(context, id + "F18", {"entities" : qUnion([Q0]), "endBound" : BoundingType.UP_TO_SURFACE, "endBoundEntityFace" : qUnion([Q1]), "depth" : 25 * mm});
        }
    });
